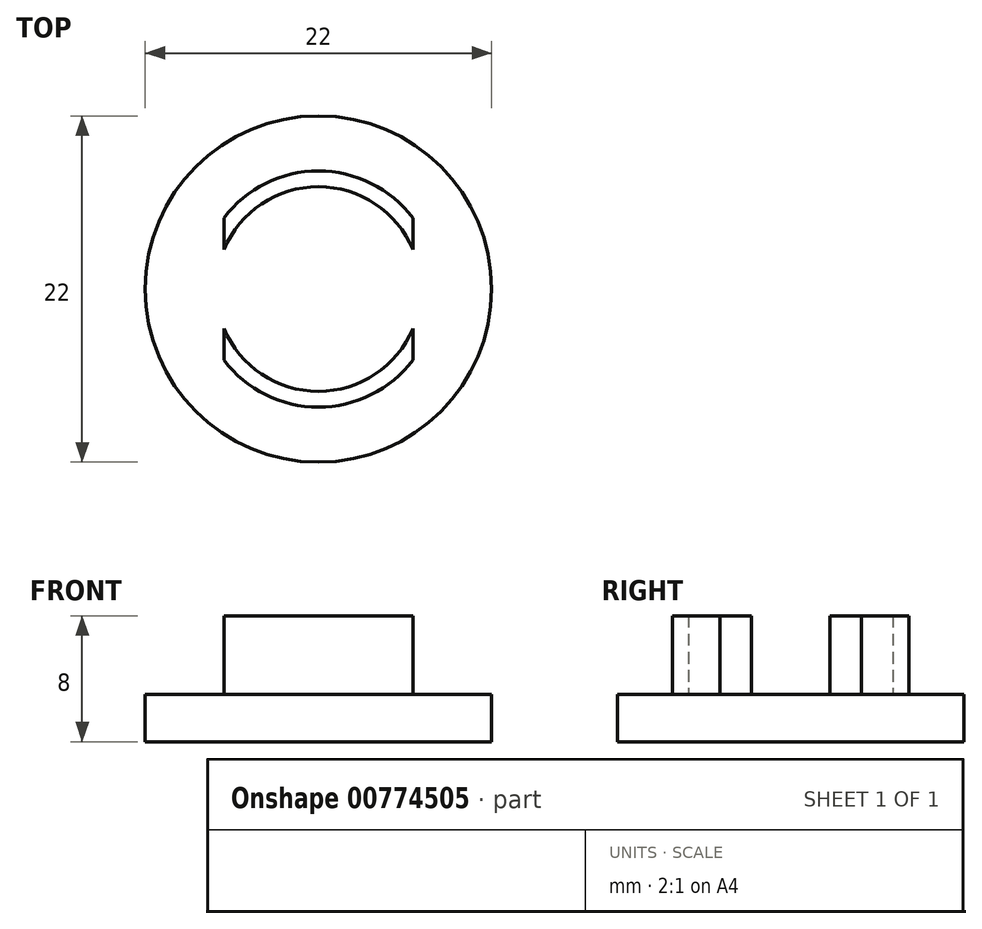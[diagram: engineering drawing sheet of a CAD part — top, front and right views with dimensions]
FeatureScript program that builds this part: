
annotation { "Feature Type Name" : "Feature", "Feature Type Description" : "" }
export const myFeature = defineFeature(function(context is Context, id is Id, definition is map)
    precondition{}
    {
        {
            var Q0;
            Q0=qCreatedBy(makeId("Top.planeOp"),FACE);
            var sketch = newSketch(context, id + "F0", { "sketchPlane" : qUnion([Q0])});
            skCircle(sketch, "E0", {"center": v(0, 0) * mm, "radius": 11 * mm});
            skSolve(sketch);
        }
        {
            var Q0;
            Q0=makeQuery(id+"F0.imprint","IMPRINT",FACE,{"disambiguationData":[TD([[makeQuery(id+"F0.imprint","IMPRINT",EDGE,{"derivedFrom":sQuery(id+"F0.wireOp",EDGE,"E0")}),1.0]])]});
            extrude(context, id + "F1", {"entities" : qUnion([Q0]), "depth" : 3 * mm, "offsetDistance" : 25 * mm});
        }
        {
            var Q0;
            Q0=makeQuery(id+"F1.opExtrude","CAP_FACE",FACE,{"disambiguationData":[OSD([sQuery(id+"F0.wireOp",EDGE,"E0")])],"isStart":false});
            var sketch = newSketch(context, id + "F2", { "sketchPlane" : qUnion([Q0])});
            skArc(sketch, "E1", {"start": v(6, 4.5) * mm, "mid": v(0, 7.5) * mm, "end": v(-6, 4.5) * mm});
            skLineSegment(sketch, "E2", {"start": v(6, 4.5) * mm, "end": v(6, -4.5) * mm});
            skLineSegment(sketch, "E3", {"start": v(-6, 4.5) * mm, "end": v(-6, -4.5) * mm});
            skPoint(sketch, "E4.orphan", {"position": v(6, -8.32) * mm});
            skPoint(sketch, "E5.orphan", {"position": v(-6, -8.32) * mm});
            skArc(sketch, "E6.trimOffspring", {"start": v(-6, -4.5) * mm, "mid": v(0, -7.5) * mm, "end": v(6, -4.5) * mm});
            skArc(sketch, "E7", {"start": v(-6, -2.5) * mm, "mid": v(0, -6.5) * mm, "end": v(6, -2.5) * mm});
            skArc(sketch, "E8.trimOffspring", {"start": v(6, 2.5) * mm, "mid": v(0, 6.5) * mm, "end": v(-6, 2.5) * mm});
            skSolve(sketch);
        }
        {
            var Q0;
            {var subQ0=sQuery(id+"F2.wireOp",EDGE,"E1");Q0=makeQuery(id+"F2.imprint","IMPRINT",FACE,{"disambiguationData":[TD([[makeQuery(id+"F2.imprint","IMPRINT",EDGE,{"derivedFrom":subQ0}),1.0]])]});}
            var Q1;
            {var subQ0=sQuery(id+"F2.wireOp",EDGE,"E6.trimOffspring");Q1=makeQuery(id+"F2.imprint","IMPRINT",FACE,{"disambiguationData":[TD([[makeQuery(id+"F2.imprint","IMPRINT",EDGE,{"derivedFrom":subQ0}),1.0]])]});}
            extrude(context, id + "F3", {"entities" : qUnion([Q0, Q1]), "operationType" : NewBodyOperationType.ADD, "depth" : 5 * mm, "offsetDistance" : 25 * mm});
        }
    });
